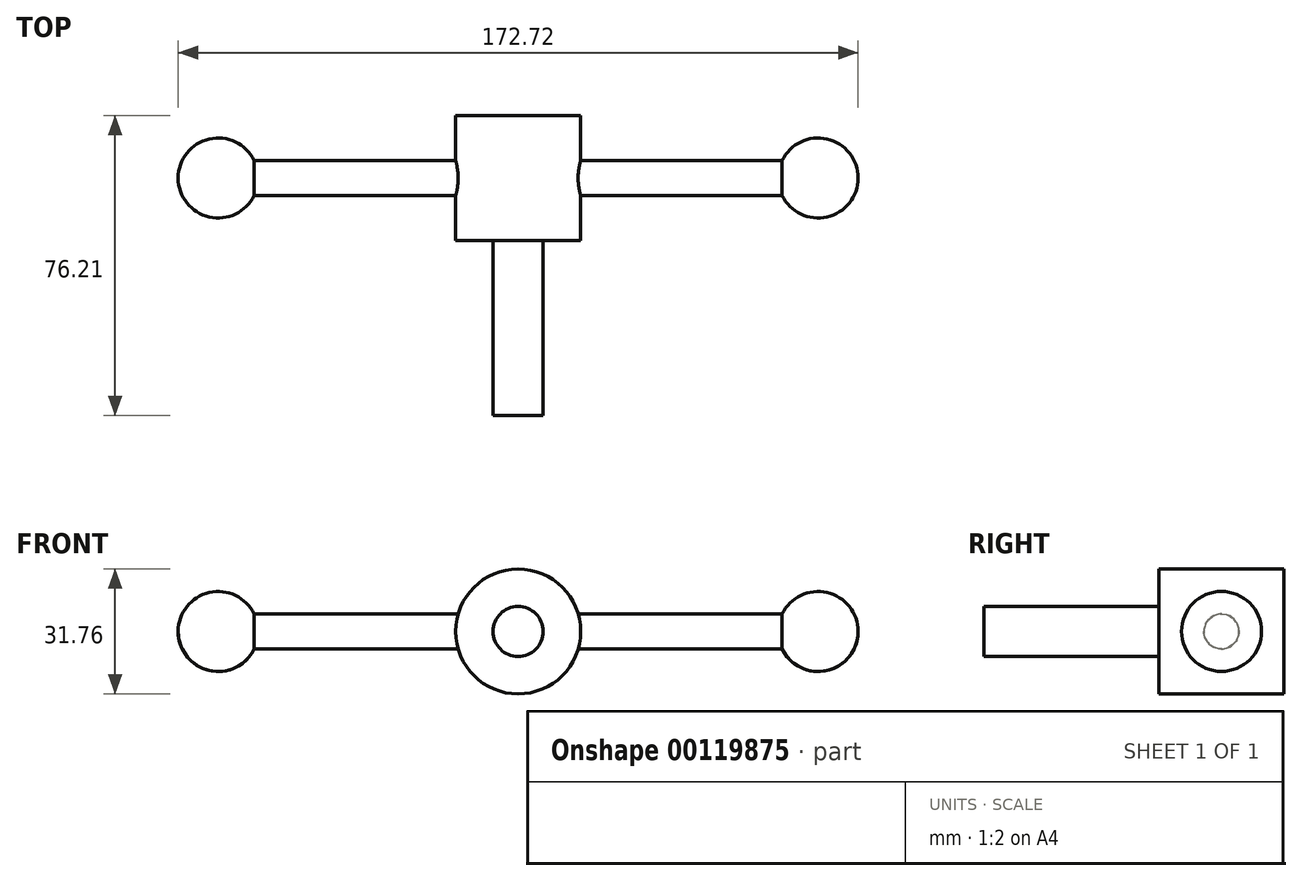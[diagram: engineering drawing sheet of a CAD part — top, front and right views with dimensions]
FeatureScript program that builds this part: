
annotation { "Feature Type Name" : "Feature", "Feature Type Description" : "" }
export const myFeature = defineFeature(function(context is Context, id is Id, definition is map)
    precondition{}
    {
        {
            var Q0;
            Q0=qCreatedBy(makeId("Front.planeOp"),FACE);
            var sketch = newSketch(context, id + "F0", { "sketchPlane" : qUnion([Q0])});
            skLineSegment(sketch, "E0", {"start": v(0, 0) * mm, "end": v(152.4, 0) * mm, "construction": true});
            skCircle(sketch, "E1", {"center": v(0, 0) * mm, "radius": 10.16 * mm});
            skCircle(sketch, "E2", {"center": v(152.4, 0) * mm, "radius": 10.16 * mm});
            skCircle(sketch, "E3", {"center": v(76.2, 0) * mm, "radius": 15.88 * mm});
            skLineSegment(sketch, "E4", {"start": v(0, 0) * mm, "end": v(152.4, 0) * mm});
            skLineSegment(sketch, "E5", {"start": v(-10.16, 0) * mm, "end": v(10.16, 0) * mm});
            skLineSegment(sketch, "E6", {"start": v(142.24, 0) * mm, "end": v(162.56, 0) * mm});
            skSolve(sketch);
        }
        {
            var Q0;
            Q0=makeQuery(id+"F0.imprint","IMPRINT",FACE,{"disambiguationData":[TD([[makeQuery(id+"F0.imprint","IMPRINT",EDGE,{"derivedFrom":sQuery(id+"F0.wireOp",EDGE,"E3")}),1.0]])]});
            extrude(context, id + "F1", {"entities" : qUnion([Q0]), "endBound" : BoundingType.SYMMETRIC, "depth" : 31.75 * mm});
        }
        {
            var Q0;
            {var subQ0=sQuery(id+"F0.wireOp",EDGE,"E5");var subQ4=makeQuery(id+"F0.imprint","IMPRINT",VERTEX,{"derivedFrom":subQ0});Q0=makeQuery(id+"F0.imprint","IMPRINT",FACE,{"disambiguationData":[TD([[makeQuery(id+"F0.imprint","IMPRINT",EDGE,{"disambiguationData":[TD([[subQ4,1.0]])],"derivedFrom":subQ0}),1.0]])]});}
            var Q1;
            {var subQ0=sQuery(id+"F0.wireOp",EDGE,"E6");var subQ4=makeQuery(id+"F0.imprint","IMPRINT",VERTEX,{"derivedFrom":subQ0});Q1=makeQuery(id+"F0.imprint","IMPRINT",FACE,{"disambiguationData":[TD([[makeQuery(id+"F0.imprint","IMPRINT",EDGE,{"disambiguationData":[TD([[subQ4,1.0]])],"derivedFrom":subQ0}),1.0]])]});}
            var Q2;
            Q2=sQuery(id+"F0.wireOp",EDGE,"E4");
            revolve(context, id + "F2", {"entities" : qUnion([Q0, Q1]), "axis" : qUnion([Q2]), "revolveType" : RevolveType.FULL});
        }
        {
            var Q0;
            Q0=qCreatedBy(makeId("Right.planeOp"),FACE);
            var sketch = newSketch(context, id + "F3", { "sketchPlane" : qUnion([Q0])});
            skCircle(sketch, "E7", {"center": v(0, 0) * mm, "radius": 4.45 * mm});
            skSolve(sketch);
        }
        {
            var Q0;
            Q0 = qSketchRegion(id + "F3", true);
            extrude(context, id + "F4", {"entities" : qUnion([Q0]), "operationType" : NewBodyOperationType.ADD, "depth" : 152.4 * mm});
        }
        {
            var Q0;
            Q0=makeQuery(id+"F1.opExtrude","CAP_FACE",FACE,{"disambiguationData":[OSD([sQuery(id+"F0.wireOp",EDGE,"E3")])],"isStart":false});
            var sketch = newSketch(context, id + "F5", { "sketchPlane" : qUnion([Q0])});
            skCircle(sketch, "E8", {"center": v(76.2, 0) * mm, "radius": 6.35 * mm});
            skSolve(sketch);
        }
        {
            var Q0;
            Q0=makeQuery(id+"F5.imprint","IMPRINT",FACE,{"disambiguationData":[TD([[makeQuery(id+"F5.imprint","IMPRINT",EDGE,{"derivedFrom":sQuery(id+"F5.wireOp",EDGE,"E8")}),1.0]])]});
            extrude(context, id + "F6", {"entities" : qUnion([Q0]), "operationType" : NewBodyOperationType.ADD, "depth" : 44.45 * mm});
        }
    });
